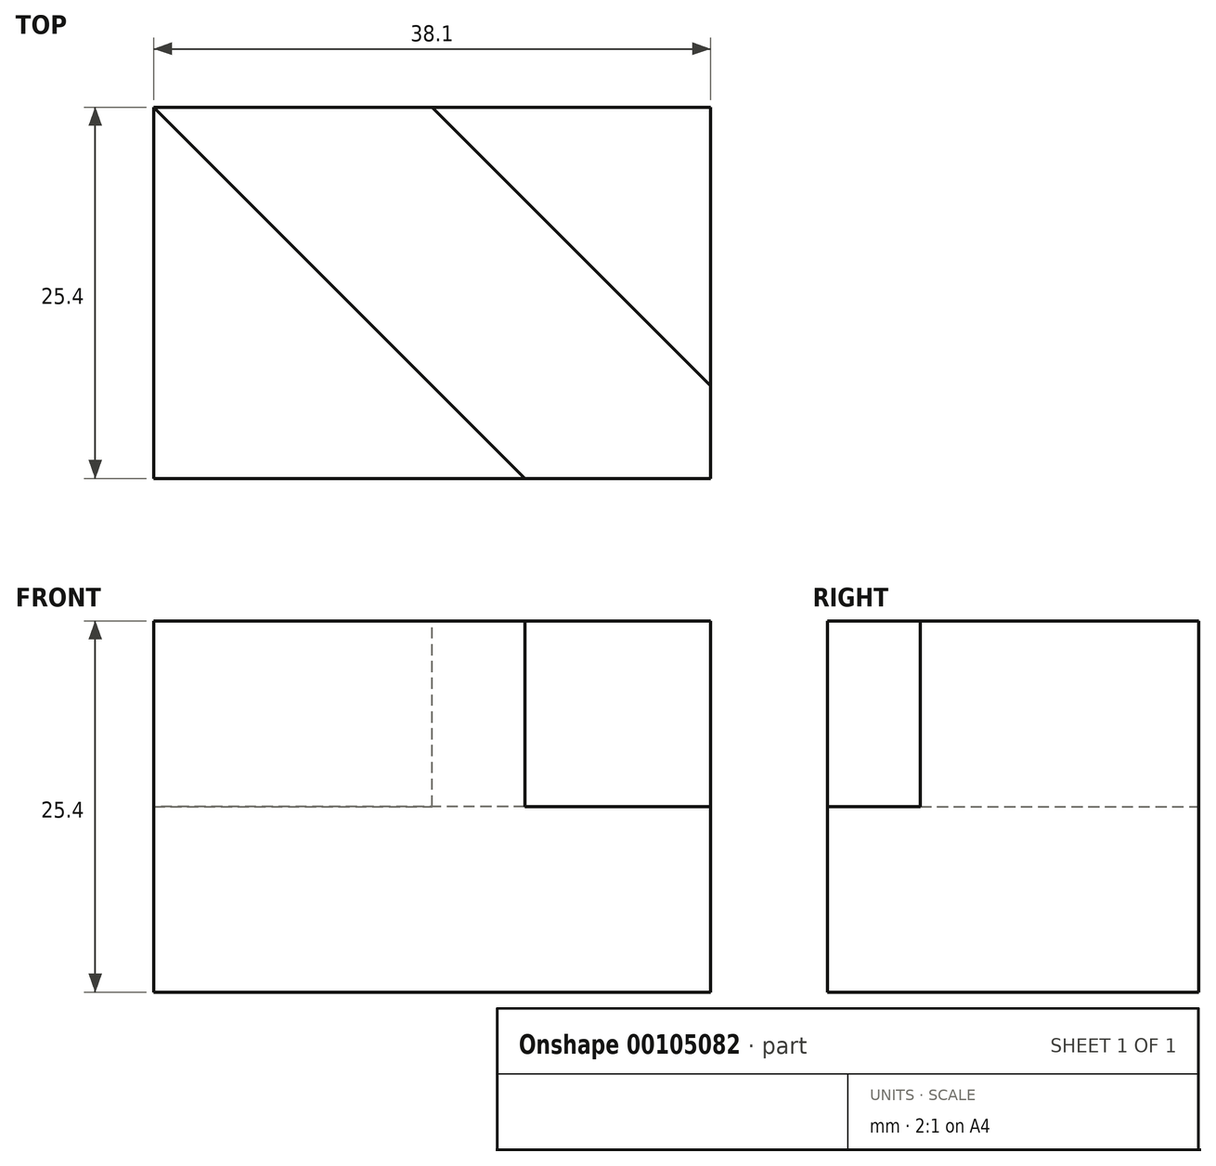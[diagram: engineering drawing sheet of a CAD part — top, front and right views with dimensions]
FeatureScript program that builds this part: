
annotation { "Feature Type Name" : "Feature", "Feature Type Description" : "" }
export const myFeature = defineFeature(function(context is Context, id is Id, definition is map)
    precondition{}
    {
        {
            var Q0;
            Q0=qCreatedBy(makeId("Front.planeOp"),FACE);
            var sketch = newSketch(context, id + "F0", { "sketchPlane" : qUnion([Q0])});
            skLineSegment(sketch, "E0.bottom", {"start": v(0, 0) * mm, "end": v(38.1, 0) * mm});
            skLineSegment(sketch, "E0.top", {"start": v(0, 25.4) * mm, "end": v(38.1, 25.4) * mm});
            skLineSegment(sketch, "E0.left", {"start": v(0, 0) * mm, "end": v(0, 25.4) * mm});
            skLineSegment(sketch, "E0.right", {"start": v(38.1, 0) * mm, "end": v(38.1, 25.4) * mm});
            skSolve(sketch);
        }
        {
            var Q0;
            Q0 = qSketchRegion(id + "F0", true);
            extrude(context, id + "F1", {"entities" : qUnion([Q0]), "depth" : 25.4 * mm});
        }
        {
            var Q0;
            Q0=makeQuery(id+"F1.opExtrude","CAP_FACE",FACE,{"disambiguationData":[OSD([sQuery(id+"F0.wireOp",EDGE,"E0.bottom"),sQuery(id+"F0.wireOp",EDGE,"E0.top"),sQuery(id+"F0.wireOp",EDGE,"E0.left"),sQuery(id+"F0.wireOp",EDGE,"E0.right")])],"isStart":false});
            var sketch = newSketch(context, id + "F2", { "sketchPlane" : qUnion([Q0])});
            skLineSegment(sketch, "E1.bottom", {"start": v(38.1, 25.4) * mm, "end": v(25.4, 25.4) * mm});
            skLineSegment(sketch, "E1.top", {"start": v(38.1, 12.7) * mm, "end": v(25.4, 12.7) * mm});
            skLineSegment(sketch, "E1.left", {"start": v(38.1, 25.4) * mm, "end": v(38.1, 12.7) * mm});
            skLineSegment(sketch, "E1.right", {"start": v(25.4, 25.4) * mm, "end": v(25.4, 12.7) * mm});
            skSolve(sketch);
        }
        {
            var Q0;
            Q0 = qSketchRegion(id + "F2", true);
            extrude(context, id + "F3", {"entities" : qUnion([Q0]), "operationType" : NewBodyOperationType.REMOVE, "oppositeDirection" : true, "depth" : 6.35 * mm});
        }
        {
            var Q0;
            Q0=makeQuery(id+"F1.opExtrude","SWEPT_FACE",FACE,{"disambiguationData":[OSD([sQuery(id+"F0.wireOp",EDGE,"E0.top")])]});
            var sketch = newSketch(context, id + "F4", { "sketchPlane" : qUnion([Q0])});
            skLineSegment(sketch, "E2", {"start": v(25.4, -25.4) * mm, "end": v(0, 0) * mm});
            skLineSegment(sketch, "E3", {"start": v(38.1, -19.05) * mm, "end": v(19.05, 0) * mm});
            skSolve(sketch);
        }
        {
            var Q0;
            {var subQ3=sQuery(id+"F4.wireOp",EDGE,"E2");Q0=makeQuery(id+"F4.imprint","IMPRINT",FACE,{"disambiguationData":[TD([[makeQuery(id+"F4.imprint","IMPRINT",EDGE,{"derivedFrom":subQ3}),-1.0]])]});}
            extrude(context, id + "F5", {"entities" : qUnion([Q0]), "operationType" : NewBodyOperationType.REMOVE, "oppositeDirection" : true, "depth" : 12.7 * mm});
        }
    });
